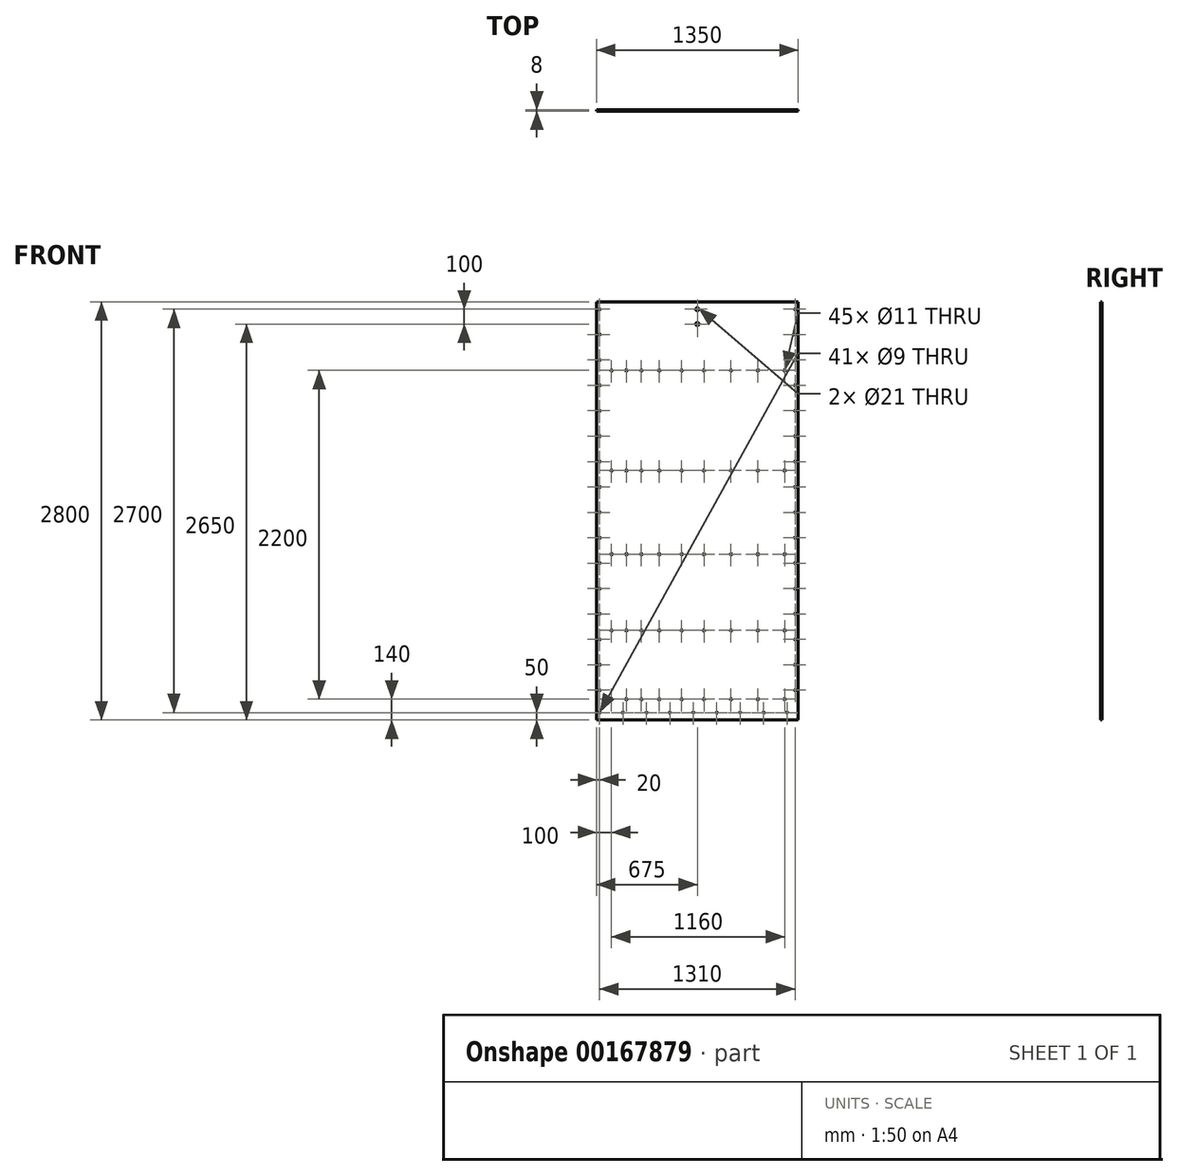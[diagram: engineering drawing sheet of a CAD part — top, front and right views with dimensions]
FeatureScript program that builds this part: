
annotation { "Feature Type Name" : "Feature", "Feature Type Description" : "" }
export const myFeature = defineFeature(function(context is Context, id is Id, definition is map)
    precondition{}
    {
        {
            var Q0;
            Q0=qCreatedBy(makeId("Front.planeOp"),FACE);
            var sketch = newSketch(context, id + "F0", { "sketchPlane" : qUnion([Q0])});
            skLineSegment(sketch, "E0.bottom", {"start": v(-1350, 1400) * mm, "end": v(0, 1400) * mm});
            skLineSegment(sketch, "E0.top", {"start": v(-1350, -1400) * mm, "end": v(0, -1400) * mm});
            skLineSegment(sketch, "E0.left", {"start": v(-1350, 1400) * mm, "end": v(-1350, -1400) * mm});
            skLineSegment(sketch, "E0.right", {"start": v(1350, 1400) * mm, "end": v(1350, -1400) * mm, "construction": true});
            skPoint(sketch, "E0.middle", {"position": v(0, 0) * mm});
            skLineSegment(sketch, "E1", {"start": v(0, 1400) * mm, "end": v(0, -1400) * mm});
            skCircle(sketch, "E2", {"center": v(-675, 1250) * mm, "radius": 10.5 * mm});
            skCircle(sketch, "E3", {"center": v(-675, 1350) * mm, "radius": 10.5 * mm});
            skLineSegment(sketch, "E4", {"start": v(0, 1400) * mm, "end": v(1350, 1400) * mm, "construction": true});
            skLineSegment(sketch, "E5", {"start": v(0, -1400) * mm, "end": v(1350, -1400) * mm, "construction": true});
            skLineSegment(sketch, "E6", {"start": v(-675, 1400) * mm, "end": v(-675, -1400) * mm, "construction": true});
            skCircle(sketch, "E7", {"center": v(-1330, 1350) * mm, "radius": 4.5 * mm});
            skCircle(sketch, "E8.0.1.0", {"center": v(-1330, 1180) * mm, "radius": 4.5 * mm});
            skCircle(sketch, "E8.0.2.0", {"center": v(-1330, 1010) * mm, "radius": 4.5 * mm});
            skCircle(sketch, "E8.0.3.0", {"center": v(-1330, 840) * mm, "radius": 4.5 * mm});
            skCircle(sketch, "E8.0.4.0", {"center": v(-1330, 670) * mm, "radius": 4.5 * mm});
            skCircle(sketch, "E8.0.5.0", {"center": v(-1330, 500) * mm, "radius": 4.5 * mm});
            skCircle(sketch, "E8.0.6.0", {"center": v(-1330, 330) * mm, "radius": 4.5 * mm});
            skCircle(sketch, "E8.0.7.0", {"center": v(-1330, 160) * mm, "radius": 4.5 * mm});
            skCircle(sketch, "E8.0.8.0", {"center": v(-1330, -10) * mm, "radius": 4.5 * mm});
            skCircle(sketch, "E8.0.9.0", {"center": v(-1330, -180) * mm, "radius": 4.5 * mm});
            skCircle(sketch, "E8.0.10.0", {"center": v(-1330, -350) * mm, "radius": 4.5 * mm});
            skCircle(sketch, "E8.0.11.0", {"center": v(-1330, -520) * mm, "radius": 4.5 * mm});
            skCircle(sketch, "E8.0.12.0", {"center": v(-1330, -690) * mm, "radius": 4.5 * mm});
            skCircle(sketch, "E8.0.13.0", {"center": v(-1330, -860) * mm, "radius": 4.5 * mm});
            skCircle(sketch, "E8.0.14.0", {"center": v(-1330, -1030) * mm, "radius": 4.5 * mm});
            skCircle(sketch, "E8.0.15.0", {"center": v(-1330, -1200) * mm, "radius": 4.5 * mm});
            skLineSegment(sketch, "E8.direction1", {"start": v(-1330, 1350) * mm, "end": v(-1305, 1350) * mm, "construction": true});
            skLineSegment(sketch, "E8.direction2", {"start": v(-1330, 1350) * mm, "end": v(-1330, 1180) * mm, "construction": true});
            skLineSegment(sketch, "E9", {"start": v(0, 0) * mm, "end": v(-1350, 0) * mm, "construction": true});
            skCircle(sketch, "E10", {"center": v(-20, 1350) * mm, "radius": 4.5 * mm});
            skCircle(sketch, "E11.0.1.0", {"center": v(-20, 1180) * mm, "radius": 4.5 * mm});
            skCircle(sketch, "E11.0.2.0", {"center": v(-20, 1010) * mm, "radius": 4.5 * mm});
            skCircle(sketch, "E11.0.3.0", {"center": v(-20, 840) * mm, "radius": 4.5 * mm});
            skCircle(sketch, "E11.0.4.0", {"center": v(-20, 670) * mm, "radius": 4.5 * mm});
            skCircle(sketch, "E11.0.5.0", {"center": v(-20, 500) * mm, "radius": 4.5 * mm});
            skCircle(sketch, "E11.0.6.0", {"center": v(-20, 330) * mm, "radius": 4.5 * mm});
            skCircle(sketch, "E11.0.7.0", {"center": v(-20, 160) * mm, "radius": 4.5 * mm});
            skCircle(sketch, "E11.0.8.0", {"center": v(-20, -10) * mm, "radius": 4.5 * mm});
            skCircle(sketch, "E11.0.9.0", {"center": v(-20, -180) * mm, "radius": 4.5 * mm});
            skCircle(sketch, "E11.0.10.0", {"center": v(-20, -350) * mm, "radius": 4.5 * mm});
            skCircle(sketch, "E11.0.11.0", {"center": v(-20, -520) * mm, "radius": 4.5 * mm});
            skCircle(sketch, "E11.0.12.0", {"center": v(-20, -690) * mm, "radius": 4.5 * mm});
            skCircle(sketch, "E11.0.13.0", {"center": v(-20, -860) * mm, "radius": 4.5 * mm});
            skCircle(sketch, "E11.0.14.0", {"center": v(-20, -1030) * mm, "radius": 4.5 * mm});
            skCircle(sketch, "E11.0.15.0", {"center": v(-20, -1200) * mm, "radius": 4.5 * mm});
            skLineSegment(sketch, "E11.direction1", {"start": v(-20, 1350) * mm, "end": v(95.78, 1350) * mm, "construction": true});
            skLineSegment(sketch, "E11.direction2", {"start": v(-20, 1350) * mm, "end": v(-20, 1180) * mm, "construction": true});
            skCircle(sketch, "E12", {"center": v(-1330, -1350) * mm, "radius": 4.5 * mm});
            skCircle(sketch, "E13.1.0.0", {"center": v(-1173, -1350) * mm, "radius": 4.5 * mm});
            skCircle(sketch, "E13.2.0.0", {"center": v(-1016, -1350) * mm, "radius": 4.5 * mm});
            skCircle(sketch, "E13.3.0.0", {"center": v(-859, -1350) * mm, "radius": 4.5 * mm});
            skCircle(sketch, "E13.4.0.0", {"center": v(-702, -1350) * mm, "radius": 4.5 * mm});
            skCircle(sketch, "E13.5.0.0", {"center": v(-545, -1350) * mm, "radius": 4.5 * mm});
            skCircle(sketch, "E13.6.0.0", {"center": v(-388, -1350) * mm, "radius": 4.5 * mm});
            skCircle(sketch, "E13.7.0.0", {"center": v(-231, -1350) * mm, "radius": 4.5 * mm});
            skCircle(sketch, "E13.8.0.0", {"center": v(-74, -1350) * mm, "radius": 4.5 * mm});
            skLineSegment(sketch, "E13.direction1", {"start": v(-1330, -1350) * mm, "end": v(-1173, -1350) * mm, "construction": true});
            skSolve(sketch);
        }
        {
            var Q0;
            Q0=makeQuery(id+"F0.imprint","IMPRINT",FACE,{"disambiguationData":[TD([[makeQuery(id+"F0.imprint","IMPRINT",EDGE,{"derivedFrom":sQuery(id+"F0.wireOp",EDGE,"E0.bottom")}),-1.0]])]});
            extrude(context, id + "F1", {"entities" : qUnion([Q0]), "endBound" : BoundingType.SYMMETRIC, "oppositeDirection" : true, "offsetDistance" : 25 * mm, "depth" : 8 * mm});
        }
        {
            var Q0;
            Q0=makeQuery(id+"F0.imprint","IMPRINT",FACE,{"disambiguationData":[TD([[makeQuery(id+"F0.imprint","IMPRINT",EDGE,{"derivedFrom":sQuery(id+"F0.wireOp",EDGE,"E0.bottom")}),-1.0]])]});
            var sketch = newSketch(context, id + "F2", { "sketchPlane" : qUnion([Q0])});
            skCircle(sketch, "E14", {"center": v(-1250, -1260) * mm, "radius": 5.5 * mm});
            skCircle(sketch, "E15", {"center": v(-1150, -1260) * mm, "radius": 5.5 * mm});
            skCircle(sketch, "E16", {"center": v(-1050, -1260) * mm, "radius": 5.5 * mm});
            skCircle(sketch, "E17", {"center": v(-930, -1260) * mm, "radius": 5.5 * mm});
            skCircle(sketch, "E18", {"center": v(-780, -1260) * mm, "radius": 5.5 * mm});
            skCircle(sketch, "E19", {"center": v(-630, -1260) * mm, "radius": 5.5 * mm});
            skCircle(sketch, "E20", {"center": v(-450, -1260) * mm, "radius": 5.5 * mm});
            skCircle(sketch, "E21", {"center": v(-90, -1260) * mm, "radius": 5.5 * mm});
            skCircle(sketch, "E22", {"center": v(-270, -1260) * mm, "radius": 5.5 * mm});
            skLineSegment(sketch, "E23", {"start": v(-1350, -1232.5) * mm, "end": v(0, -1232.5) * mm, "construction": true});
            skLineSegment(sketch, "E24", {"start": v(-1350, -1287.5) * mm, "end": v(0, -1287.5) * mm, "construction": true});
            skCircle(sketch, "E25", {"center": v(-1250, -800) * mm, "radius": 5.5 * mm});
            skCircle(sketch, "E26", {"center": v(-1150, -800) * mm, "radius": 5.5 * mm});
            skCircle(sketch, "E27", {"center": v(-1050, -800) * mm, "radius": 5.5 * mm});
            skCircle(sketch, "E28", {"center": v(-930, -800) * mm, "radius": 5.5 * mm});
            skCircle(sketch, "E29", {"center": v(-780, -800) * mm, "radius": 5.5 * mm});
            skCircle(sketch, "E30", {"center": v(-630, -800) * mm, "radius": 5.5 * mm});
            skCircle(sketch, "E31", {"center": v(-450, -800) * mm, "radius": 5.5 * mm});
            skCircle(sketch, "E32", {"center": v(-90, -800) * mm, "radius": 5.5 * mm});
            skCircle(sketch, "E33", {"center": v(-270, -800) * mm, "radius": 5.5 * mm});
            skLineSegment(sketch, "E34", {"start": v(-1350, -772.5) * mm, "end": v(0, -772.5) * mm, "construction": true});
            skLineSegment(sketch, "E35", {"start": v(-1350, -827.5) * mm, "end": v(0, -827.5) * mm, "construction": true});
            skCircle(sketch, "E36", {"center": v(-1250, -290) * mm, "radius": 5.5 * mm});
            skCircle(sketch, "E37", {"center": v(-1150, -290) * mm, "radius": 5.5 * mm});
            skCircle(sketch, "E38", {"center": v(-1050, -290) * mm, "radius": 5.5 * mm});
            skCircle(sketch, "E39", {"center": v(-930, -290) * mm, "radius": 5.5 * mm});
            skCircle(sketch, "E40", {"center": v(-780, -290) * mm, "radius": 5.5 * mm});
            skCircle(sketch, "E41", {"center": v(-630, -290) * mm, "radius": 5.5 * mm});
            skCircle(sketch, "E42", {"center": v(-450, -290) * mm, "radius": 5.5 * mm});
            skCircle(sketch, "E43", {"center": v(-90, -290) * mm, "radius": 5.5 * mm});
            skCircle(sketch, "E44", {"center": v(-270, -290) * mm, "radius": 5.5 * mm});
            skLineSegment(sketch, "E45", {"start": v(-1350, -262.5) * mm, "end": v(0, -262.5) * mm, "construction": true});
            skLineSegment(sketch, "E46", {"start": v(-1350, -317.5) * mm, "end": v(0, -317.5) * mm, "construction": true});
            skCircle(sketch, "E47", {"center": v(-1250, 270) * mm, "radius": 5.5 * mm});
            skCircle(sketch, "E48", {"center": v(-1150, 270) * mm, "radius": 5.5 * mm});
            skCircle(sketch, "E49", {"center": v(-1050, 270) * mm, "radius": 5.5 * mm});
            skCircle(sketch, "E50", {"center": v(-930, 270) * mm, "radius": 5.5 * mm});
            skCircle(sketch, "E51", {"center": v(-780, 270) * mm, "radius": 5.5 * mm});
            skCircle(sketch, "E52", {"center": v(-630, 270) * mm, "radius": 5.5 * mm});
            skCircle(sketch, "E53", {"center": v(-450, 270) * mm, "radius": 5.5 * mm});
            skCircle(sketch, "E54", {"center": v(-90, 270) * mm, "radius": 5.5 * mm});
            skCircle(sketch, "E55", {"center": v(-270, 270) * mm, "radius": 5.5 * mm});
            skLineSegment(sketch, "E56", {"start": v(-1350, 297.5) * mm, "end": v(0, 297.5) * mm, "construction": true});
            skLineSegment(sketch, "E57", {"start": v(-1350, 242.5) * mm, "end": v(0, 242.5) * mm, "construction": true});
            skCircle(sketch, "E58", {"center": v(-1250, 940) * mm, "radius": 5.5 * mm});
            skCircle(sketch, "E59", {"center": v(-1150, 940) * mm, "radius": 5.5 * mm});
            skCircle(sketch, "E60", {"center": v(-1050, 940) * mm, "radius": 5.5 * mm});
            skCircle(sketch, "E61", {"center": v(-930, 940) * mm, "radius": 5.5 * mm});
            skCircle(sketch, "E62", {"center": v(-780, 940) * mm, "radius": 5.5 * mm});
            skCircle(sketch, "E63", {"center": v(-630, 940) * mm, "radius": 5.5 * mm});
            skCircle(sketch, "E64", {"center": v(-450, 940) * mm, "radius": 5.5 * mm});
            skCircle(sketch, "E65", {"center": v(-90, 940) * mm, "radius": 5.5 * mm});
            skCircle(sketch, "E66", {"center": v(-270, 940) * mm, "radius": 5.5 * mm});
            skLineSegment(sketch, "E67", {"start": v(-1350, 967.5) * mm, "end": v(0, 967.5) * mm, "construction": true});
            skLineSegment(sketch, "E68", {"start": v(-1350, 912.5) * mm, "end": v(0, 912.5) * mm, "construction": true});
            skSolve(sketch);
        }
        {
            var Q0;
            Q0 = qSketchRegion(id + "F2", true);
            extrude(context, id + "F3", {"entities" : qUnion([Q0]), "operationType" : NewBodyOperationType.REMOVE, "endBound" : BoundingType.SYMMETRIC, "depth" : 25 * mm, "offsetDistance" : 25 * mm});
        }
    });
